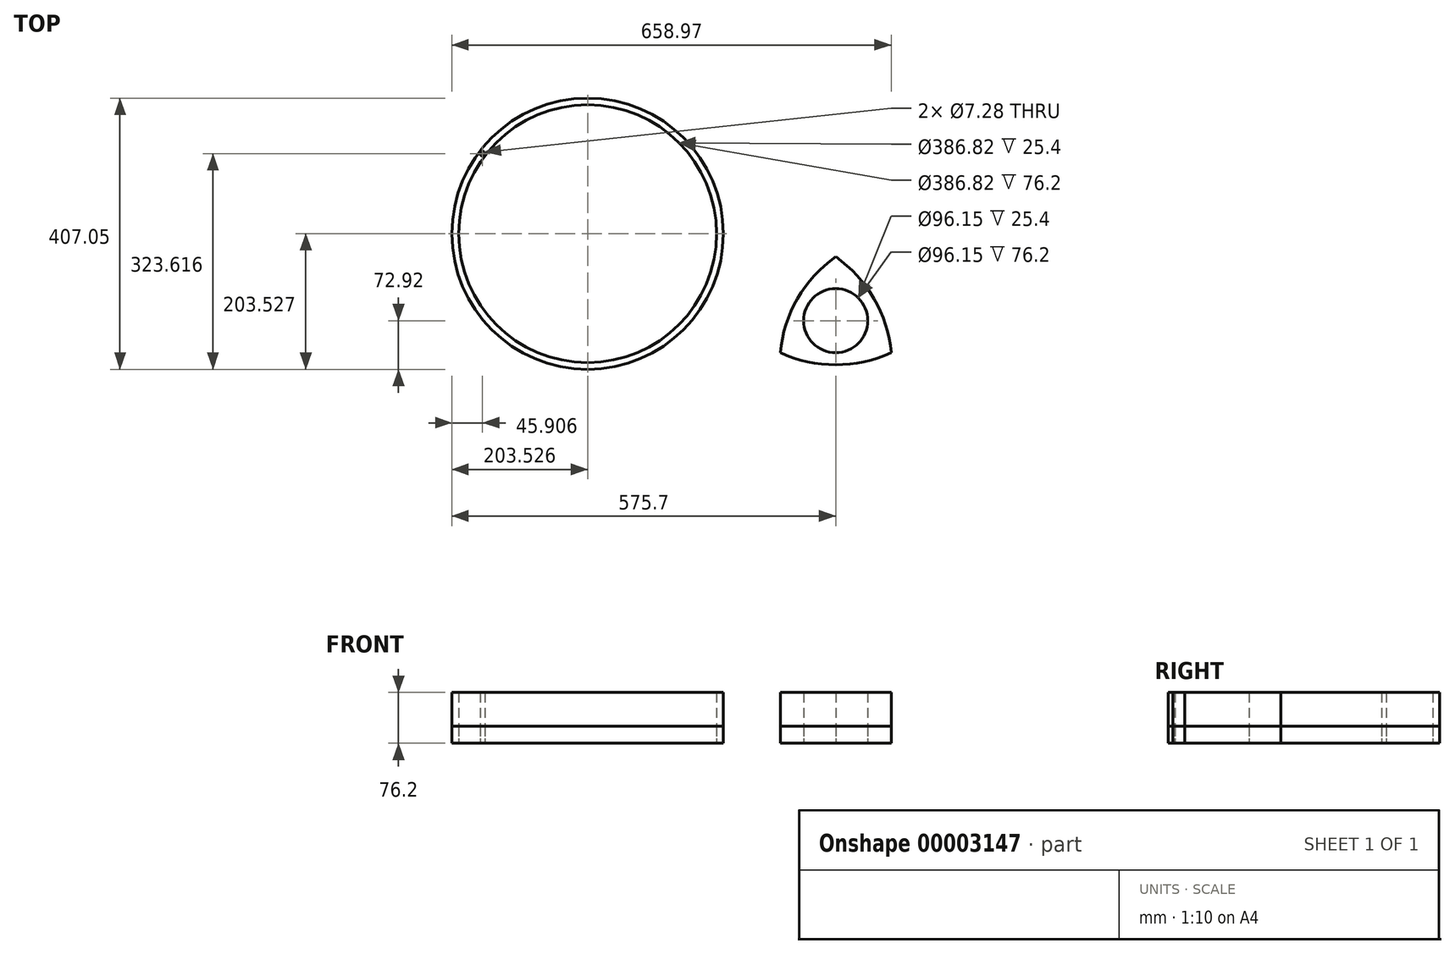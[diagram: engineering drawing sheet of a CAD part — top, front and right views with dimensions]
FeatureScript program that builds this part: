
annotation { "Feature Type Name" : "Feature", "Feature Type Description" : "" }
export const myFeature = defineFeature(function(context is Context, id is Id, definition is map)
    precondition{}
    {
        {
            var Q0;
            Q0=qCreatedBy(makeId("Top.planeOp"),FACE);
            var sketch = newSketch(context, id + "F0", { "sketchPlane" : qUnion([Q0])});
            skCircle(sketch, "E0.cCircle", {"center": v(0, 0) * mm, "radius": 48.08 * mm});
            skLineSegment(sketch, "E0.0", {"start": v(83.27, -48.08) * mm, "end": v(-83.27, -48.08) * mm});
            skLineSegment(sketch, "E0.1", {"start": v(-83.27, -48.08) * mm, "end": v(0, 96.15) * mm});
            skLineSegment(sketch, "E0.2", {"start": v(83.27, -48.08) * mm, "end": v(0, 96.15) * mm});
            skPoint(sketch, "E0.0.midPoint", {"position": v(0, -48.08) * mm});
            skLineSegment(sketch, "E1", {"start": v(0, 149.08) * mm, "end": v(0, -181.27) * mm, "construction": true});
            skLineSegment(sketch, "E2", {"start": v(-330.92, -191.06) * mm, "end": v(285.86, 165.04) * mm, "construction": true});
            skLineSegment(sketch, "E3", {"start": v(-270.9, 156.4) * mm, "end": v(156.73, -90.49) * mm, "construction": true});
            skArc(sketch, "E4", {"start": v(0, 96.15) * mm, "mid": v(-57.32, 33.1) * mm, "end": v(-83.27, -48.08) * mm});
            skPoint(sketch, "E4.third.point", {"position": v(194.44, -112.26) * mm});
            skPoint(sketch, "E5.third.point", {"position": v(-228.85, -132.13) * mm});
            skArc(sketch, "E6", {"start": v(-83.27, -48.08) * mm, "mid": v(0, -66.19) * mm, "end": v(83.27, -48.08) * mm});
            skPoint(sketch, "E6.third.point", {"position": v(0, 334.81) * mm});
            skArc(sketch, "E7.trimOffspring", {"start": v(83.27, -48.08) * mm, "mid": v(57.32, 33.1) * mm, "end": v(0, 96.15) * mm});
            skCircle(sketch, "E8", {"center": v(-372.17, 130.6) * mm, "radius": 203.53 * mm});
            skCircle(sketch, "E9", {"center": v(-372.17, 130.6) * mm, "radius": 193.41 * mm});
            skCircle(sketch, "E10", {"center": v(-529.8, 250.7) * mm, "radius": 3.64 * mm});
            skSolve(sketch);
        }
        {
            var Q0;
            {var subQ0=sQuery(id+"F0.wireOp",EDGE,"E6");var subQ2=sQuery(id+"F0.wireOp",EDGE,"E0.cCircle");var subQ4=sQuery(id+"F0.wireOp",EDGE,"E0.1");var subQ5=sQuery(id+"F0.wireOp",EDGE,"E4");var subQ8=sQuery(id+"F0.wireOp",EDGE,"E0.2");var subQ9=sQuery(id+"F0.wireOp",EDGE,"E7.trimOffspring");var subQ12=makeQuery(id+"F0.imprint","INTERSECT",VERTEX,{"derivedFrom":[subQ2,subQ4]});var subQ16=makeQuery(id+"F0.imprint","INTERSECT",VERTEX,{"derivedFrom":[subQ2,subQ8]});Q0=qUnion([makeQuery(id+"F0.imprint","IMPRINT",FACE,{"disambiguationData":[TD([[makeQuery(id+"F0.imprint","IMPRINT",EDGE,{"derivedFrom":subQ0}),1.0]])]}),makeQuery(id+"F0.imprint","IMPRINT",FACE,{"disambiguationData":[TD([[makeQuery(id+"F0.imprint","IMPRINT",EDGE,{"derivedFrom":subQ5}),1.0]])]}),makeQuery(id+"F0.imprint","IMPRINT",FACE,{"disambiguationData":[TD([[makeQuery(id+"F0.imprint","IMPRINT",EDGE,{"derivedFrom":subQ9}),1.0]])]}),makeQuery(id+"F0.imprint","IMPRINT",FACE,{"disambiguationData":[TD([[makeQuery(id+"F0.imprint","IMPRINT",EDGE,{"disambiguationData":[TD([[subQ12,1.0]])],"derivedFrom":subQ2}),-1.0]])]}),makeQuery(id+"F0.imprint","IMPRINT",FACE,{"disambiguationData":[TD([[makeQuery(id+"F0.imprint","IMPRINT",EDGE,{"disambiguationData":[TD([[subQ12,-1.0]])],"derivedFrom":subQ2}),-1.0]])]}),makeQuery(id+"F0.imprint","IMPRINT",FACE,{"disambiguationData":[TD([[makeQuery(id+"F0.imprint","IMPRINT",EDGE,{"disambiguationData":[TD([[subQ16,1.0]])],"derivedFrom":subQ2}),-1.0]])]}),makeQuery(id+"F0.imprint","IMPRINT",FACE,{"disambiguationData":[TD([[makeQuery(id+"F0.imprint","IMPRINT",EDGE,{"derivedFrom":sQuery(id+"F0.wireOp",EDGE,"E8")}),1.0]])]})]);}
            extrude(context, id + "F1", {"entities" : qUnion([Q0]), "depth" : 76.2 * mm});
        }
        {
            var Q0;
            {var subQ0=sQuery(id+"F0.wireOp",EDGE,"E6");var subQ2=sQuery(id+"F0.wireOp",EDGE,"E0.cCircle");var subQ4=sQuery(id+"F0.wireOp",EDGE,"E0.1");var subQ5=sQuery(id+"F0.wireOp",EDGE,"E4");var subQ8=sQuery(id+"F0.wireOp",EDGE,"E0.2");var subQ9=sQuery(id+"F0.wireOp",EDGE,"E7.trimOffspring");var subQ12=makeQuery(id+"F0.imprint","INTERSECT",VERTEX,{"derivedFrom":[subQ2,subQ4]});var subQ16=makeQuery(id+"F0.imprint","INTERSECT",VERTEX,{"derivedFrom":[subQ2,subQ8]});Q0=qUnion([makeQuery(id+"F0.imprint","IMPRINT",FACE,{"disambiguationData":[TD([[makeQuery(id+"F0.imprint","IMPRINT",EDGE,{"derivedFrom":subQ0}),1.0]])]}),makeQuery(id+"F0.imprint","IMPRINT",FACE,{"disambiguationData":[TD([[makeQuery(id+"F0.imprint","IMPRINT",EDGE,{"derivedFrom":subQ5}),1.0]])]}),makeQuery(id+"F0.imprint","IMPRINT",FACE,{"disambiguationData":[TD([[makeQuery(id+"F0.imprint","IMPRINT",EDGE,{"derivedFrom":subQ9}),1.0]])]}),makeQuery(id+"F0.imprint","IMPRINT",FACE,{"disambiguationData":[TD([[makeQuery(id+"F0.imprint","IMPRINT",EDGE,{"disambiguationData":[TD([[subQ12,1.0]])],"derivedFrom":subQ2}),-1.0]])]}),makeQuery(id+"F0.imprint","IMPRINT",FACE,{"disambiguationData":[TD([[makeQuery(id+"F0.imprint","IMPRINT",EDGE,{"disambiguationData":[TD([[subQ12,-1.0]])],"derivedFrom":subQ2}),-1.0]])]}),makeQuery(id+"F0.imprint","IMPRINT",FACE,{"disambiguationData":[TD([[makeQuery(id+"F0.imprint","IMPRINT",EDGE,{"disambiguationData":[TD([[subQ16,1.0]])],"derivedFrom":subQ2}),-1.0]])]}),makeQuery(id+"F0.imprint","IMPRINT",FACE,{"disambiguationData":[TD([[makeQuery(id+"F0.imprint","IMPRINT",EDGE,{"derivedFrom":sQuery(id+"F0.wireOp",EDGE,"E8")}),1.0]])]})]);}
            extrude(context, id + "F2", {"entities" : qUnion([Q0]), "depth" : 25.4 * mm});
        }
        {
            var Q0;
            {var subQ0=sQuery(id+"F0.wireOp",EDGE,"E6");var subQ2=sQuery(id+"F0.wireOp",EDGE,"E0.cCircle");var subQ4=sQuery(id+"F0.wireOp",EDGE,"E0.1");var subQ5=sQuery(id+"F0.wireOp",EDGE,"E4");var subQ8=sQuery(id+"F0.wireOp",EDGE,"E0.2");var subQ9=sQuery(id+"F0.wireOp",EDGE,"E7.trimOffspring");var subQ12=makeQuery(id+"F0.imprint","INTERSECT",VERTEX,{"derivedFrom":[subQ2,subQ4]});var subQ16=makeQuery(id+"F0.imprint","INTERSECT",VERTEX,{"derivedFrom":[subQ2,subQ8]});Q0=qUnion([makeQuery(id+"F0.imprint","IMPRINT",FACE,{"disambiguationData":[TD([[makeQuery(id+"F0.imprint","IMPRINT",EDGE,{"derivedFrom":subQ0}),1.0]])]}),makeQuery(id+"F0.imprint","IMPRINT",FACE,{"disambiguationData":[TD([[makeQuery(id+"F0.imprint","IMPRINT",EDGE,{"derivedFrom":subQ5}),1.0]])]}),makeQuery(id+"F0.imprint","IMPRINT",FACE,{"disambiguationData":[TD([[makeQuery(id+"F0.imprint","IMPRINT",EDGE,{"derivedFrom":subQ9}),1.0]])]}),makeQuery(id+"F0.imprint","IMPRINT",FACE,{"disambiguationData":[TD([[makeQuery(id+"F0.imprint","IMPRINT",EDGE,{"disambiguationData":[TD([[subQ12,1.0]])],"derivedFrom":subQ2}),-1.0]])]}),makeQuery(id+"F0.imprint","IMPRINT",FACE,{"disambiguationData":[TD([[makeQuery(id+"F0.imprint","IMPRINT",EDGE,{"disambiguationData":[TD([[subQ12,-1.0]])],"derivedFrom":subQ2}),-1.0]])]}),makeQuery(id+"F0.imprint","IMPRINT",FACE,{"disambiguationData":[TD([[makeQuery(id+"F0.imprint","IMPRINT",EDGE,{"disambiguationData":[TD([[subQ16,1.0]])],"derivedFrom":subQ2}),-1.0]])]}),makeQuery(id+"F0.imprint","IMPRINT",FACE,{"disambiguationData":[TD([[makeQuery(id+"F0.imprint","IMPRINT",EDGE,{"derivedFrom":sQuery(id+"F0.wireOp",EDGE,"E8")}),1.0]])]})]);}
            extrude(context, id + "F3", {"entities" : qUnion([Q0]), "operationType" : NewBodyOperationType.REMOVE, "endBound" : BoundingType.THROUGH_ALL, "oppositeDirection" : true, "depth" : 25.4 * mm});
        }
    });
